# Revit family: equip-water-cooler-hlsy-tylr-hcrfer
name_source: partatom
category: Plumbing Fixtures
units: mm (PartAtom-declared; Revit-internal decimal feet)

## family parameters
Always vertical = Yes
Cut with Voids When Loaded = No
OmniClass Number = 23.45.00.00
OmniClass Title = Sanitary, Laundry, and Cleaning Equipment
Part Type = Normal
Room Calculation Point = No
Round Connector Dimension = Use Radius
Shared = No
Work Plane-Based = No

## types (10) — shared parameters
Apparent Load Phase 1 = 0 VA
Basin Material = Metal - Steel - Stainless - Chrome
Bubbler = Double Bubbler
Bubbler Material = Metal - Steel - Stainless - Chrome
Button Material = Metal - Steel - Stainless - Chrome
CW Connection = Yes
Chiller Option = Yes
Cooler Depth = 1' - 6 5/8"
Cooler Separation = 0' - 6 5/8"
Cooler Width = 1' - 0 1/8"
Description = Water Cooler
Dispenser Height = 2' - 0"
Filter = **ACC(HWF 172)
Glass Filter = -
HW Connection = No
Lower Cooler Rim Height = 2' - 4 3/8"
Lower Orifice Height = 2' - 6"
Manufacturer = Halsey Taylor
Number of Poles = 1
Orifice to Rim = 0' - 1 5/8"
Rim to Dispenser = 0' - 4 3/8"
Sanitary Service Size Radius = 0' - 0 5/8"
URL = http://www.halseytaylor.com
Vent Connection = No
Version = 1.0.0.0
Voltage = 0 V
Volts/Hertz = 115V/60Hz
Wall Plate Material = Metal - Steel - Stainless - Chrome
Waste Connection = Yes
Water Service Flow = 0 GPM
Water Service Flow Out = 0 GPM
Water Service Size Radius = 0' - 0 1/4"
zero-valued in all types: Power Factor

## per-type parameters (varying)
| type | Activation | Back Panel | Chiller | Fountain | Freeze Resistant | Model | Mounting | Mounting Plate | Specification URL | Type |
| HCRF-EBP FTN | Pushbutton | Yes |  |  |  | HCRF-EBP FTN |  | Incl Surface Mtg Plate | http://www.halseytaylor.com | Single-Extended |
| HRF-E FTN | Pushbutton |  |  |  | See 7633007683 | HRF-E FTN |  | In-Wall ACC | http://www.halseytaylor.com | Single-Extended |
| HRF-S FTN (not ADA) | Pushbutton |  |  |  | See 7633007783 | HRF-S FTN (not ADA) |  | In-Wall ACC | http://www.halseytaylor.com | Single-short (Not ADA) |
| HRF-EBP FTN | Pushbutton | Yes |  |  | See 7633008683 | HRF-EBP FTN |  | Incl Surface Mtg Plate | http://www.halseytaylor.com | Single-Extended |
| HRF-SBP FTN (not ADA) | Pushbutton | Yes |  |  |  | HRF-SBP FTN (not ADA) |  | Incl Surface Mtg Plate |  | Single-Short (Not ADA) |
| HCRF-ER | Pushbutton | Yes | 8214080073 (SJ8) | 7433089683 |  | HCRF-ER | HCRFSGLFRM |  | http://www.halseytaylor.com | Single (Child ADA) |
| HRF-ER | Pushbutton | Yes | 8214080073 (SJ8) | 7433083683 |  | HRF-ER | 734214851551 (Single Frame) |  | http://www.halseytaylor.com | Single |
| HRF-EREE | Sensors | Yes | 8214080073 (SJ8) | 7433087383 |  | HRF-EREE | 734214851551 (Single Frame) |  | http://www.halseytaylor.com | Single |
| HRFG-ER BO/SS | Pushbutton | Yes | 8214080073 (SJ8) | 7433084183 |  | HRFG-ER | 734214851551 (Single Frame) |  | http://www.halseytaylor.com | Single |
| HRFG-ER GG/SS | Pushbutton | Yes | 8214080073 (SJ8) | 7433082683 |  | HRFG-ER | 734214851551 (Single Frame) |  | http://www.halseytaylor.com | Single |

## geometry (parser evidence)
native form markers: Sweep x6
no freeform markers — native parametric forms only
